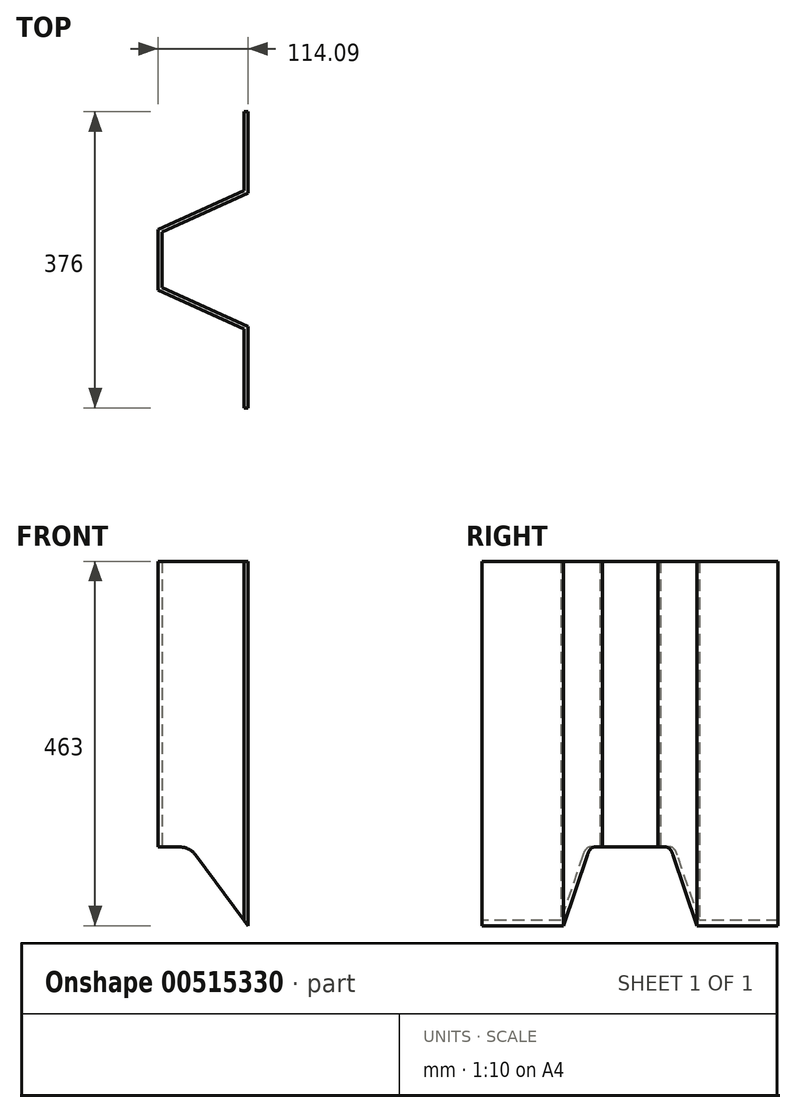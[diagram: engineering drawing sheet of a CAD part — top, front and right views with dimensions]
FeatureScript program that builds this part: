
annotation { "Feature Type Name" : "Feature", "Feature Type Description" : "" }
export const myFeature = defineFeature(function(context is Context, id is Id, definition is map)
    precondition{}
    {
        {
            var Q0;
            Q0=qCreatedBy(makeId("Top.planeOp"),FACE);
            var sketch = newSketch(context, id + "F0", { "sketchPlane" : qUnion([Q0])});
            skLineSegment(sketch, "E0", {"start": v(0, 0) * mm, "end": v(-108.5, 0) * mm, "construction": true});
            skLineSegment(sketch, "E1", {"start": v(0, 188) * mm, "end": v(0, 85) * mm});
            skLineSegment(sketch, "E2", {"start": v(0, 85) * mm, "end": v(-109.09, 35) * mm});
            skLineSegment(sketch, "E3", {"start": v(-109.09, 35) * mm, "end": v(-109.09, -35) * mm});
            skLineSegment(sketch, "E4", {"start": v(-109.09, -35) * mm, "end": v(0, -85) * mm});
            skLineSegment(sketch, "E5", {"start": v(0, -85) * mm, "end": v(0, -188) * mm});
            skLineSegment(sketch, "E6.0", {"start": v(-5, -88.2) * mm, "end": v(-5, -188) * mm});
            skLineSegment(sketch, "E6.1", {"start": v(-5, 188) * mm, "end": v(-5, 88.2) * mm});
            skLineSegment(sketch, "E6.2", {"start": v(-5, 88.2) * mm, "end": v(-114.09, 38.2) * mm});
            skLineSegment(sketch, "E6.3", {"start": v(-114.09, 38.2) * mm, "end": v(-114.09, -38.2) * mm});
            skLineSegment(sketch, "E6.4", {"start": v(-114.09, -38.2) * mm, "end": v(-5, -88.2) * mm});
            skLineSegment(sketch, "E7", {"start": v(-5, 188) * mm, "end": v(0, 188) * mm});
            skLineSegment(sketch, "E8", {"start": v(-5, -188) * mm, "end": v(0, -188) * mm});
            skSolve(sketch);
        }
        {
            var Q0;
            Q0=makeQuery(id+"F0.imprint","IMPRINT",FACE,{"disambiguationData":[TD([[makeQuery(id+"F0.imprint","IMPRINT",EDGE,{"derivedFrom":sQuery(id+"F0.wireOp",EDGE,"E1")}),-1.0]])]});
            var Q1;
            Q1=sQuery(id+"F0.wireOp",EDGE,"E2");
            var Q2;
            Q2=sQuery(id+"F0.wireOp",EDGE,"E4");
            extrude(context, id + "F1", {"entities" : qUnion([Q0]), "surfaceEntities" : qUnion([Q1, Q2]), "endBound" : BoundingType.SYMMETRIC, "depth" : 463 * mm, "offsetDistance" : 25 * mm});
        }
        {
            var Q0;
            Q0=qCreatedBy(makeId("Front.planeOp"),FACE);
            var sketch = newSketch(context, id + "F2", { "sketchPlane" : qUnion([Q0])});
            skLineSegment(sketch, "E9", {"start": v(-66.6, -141.62) * mm, "end": v(0, -231.5) * mm});
            skLineSegment(sketch, "E10", {"start": v(-114.09, -131.5) * mm, "end": v(-114.09, -231.5) * mm});
            skLineSegment(sketch, "E11", {"start": v(-114.09, -231.5) * mm, "end": v(0, -231.5) * mm});
            skPoint(sketch, "E12.0", {"position": v(0, -231.5) * mm});
            skLineSegment(sketch, "E13.0", {"start": v(-114.09, 231.5) * mm, "end": v(-114.09, -231.5) * mm, "construction": true});
            skLineSegment(sketch, "E14", {"start": v(-114.09, -131.5) * mm, "end": v(-86.68, -131.5) * mm});
            skPoint(sketch, "E15.visualSharp", {"position": v(-74.09, -131.5) * mm});
            skArc(sketch, "E15.filletArc", {"start": v(-66.6, -141.62) * mm, "mid": v(-75.43, -134.17) * mm, "end": v(-86.68, -131.5) * mm});
            skSolve(sketch);
        }
        {
            var Q0;
            Q0 = qSketchRegion(id + "F2", true);
            extrude(context, id + "F3", {"entities" : qUnion([Q0]), "operationType" : NewBodyOperationType.REMOVE, "endBound" : BoundingType.SYMMETRIC, "depth" : 400 * mm, "offsetDistance" : 25 * mm});
        }
    });
